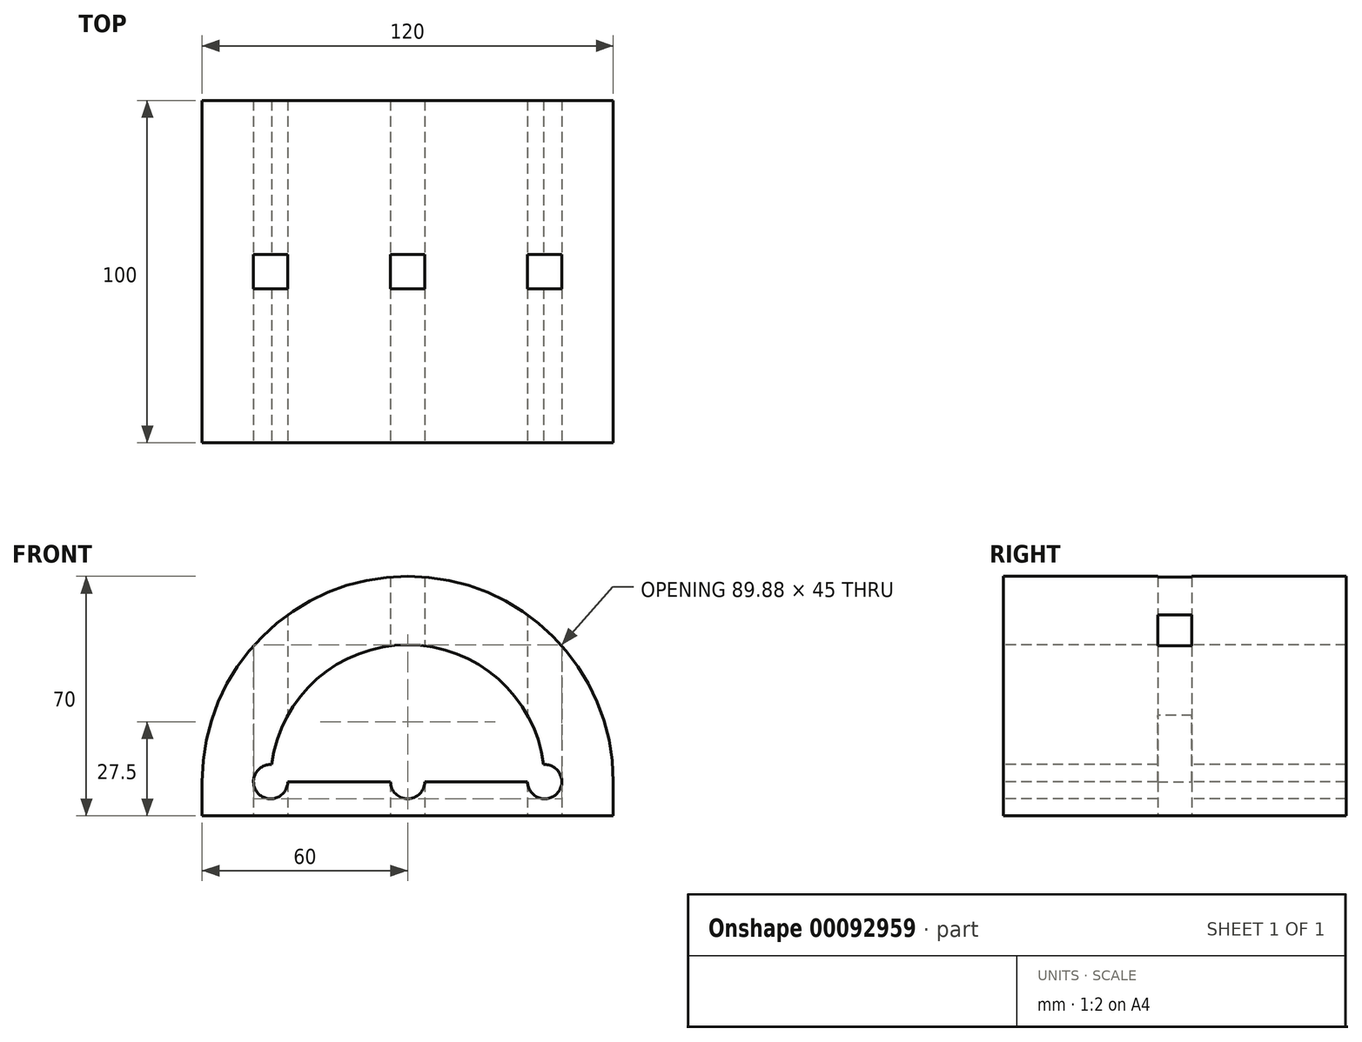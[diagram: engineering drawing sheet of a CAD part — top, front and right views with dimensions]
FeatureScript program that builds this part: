
annotation { "Feature Type Name" : "Feature", "Feature Type Description" : "" }
export const myFeature = defineFeature(function(context is Context, id is Id, definition is map)
    precondition{}
    {
        {
            var Q0;
            Q0=qCreatedBy(makeId("Top.planeOp"),FACE);
            var sketch = newSketch(context, id + "F0", { "sketchPlane" : qUnion([Q0])});
            skLineSegment(sketch, "E0.bottom", {"start": v(60, -50) * mm, "end": v(-60, -50) * mm});
            skLineSegment(sketch, "E0.top", {"start": v(60, 50) * mm, "end": v(-60, 50) * mm});
            skLineSegment(sketch, "E0.left", {"start": v(60, -50) * mm, "end": v(60, 50) * mm});
            skLineSegment(sketch, "E0.right", {"start": v(-60, -50) * mm, "end": v(-60, 50) * mm});
            skPoint(sketch, "E0.middle", {"position": v(0, 0) * mm});
            skSolve(sketch);
        }
        {
            var Q0;
            Q0 = qSketchRegion(id + "F0", true);
            extrude(context, id + "F1", {"entities" : qUnion([Q0]), "depth" : 10 * mm});
        }
        {
            var Q0;
            Q0=makeQuery(id+"F1.opExtrude","SWEPT_FACE",FACE,{"disambiguationData":[OSD([sQuery(id+"F0.wireOp",EDGE,"E0.bottom")])]});
            var sketch = newSketch(context, id + "F2", { "sketchPlane" : qUnion([Q0])});
            skArc(sketch, "E1", {"start": v(60, 10) * mm, "mid": v(0, 70) * mm, "end": v(-60, 10) * mm});
            skLineSegment(sketch, "E2", {"start": v(-60, 10) * mm, "end": v(60, 10) * mm});
            skSolve(sketch);
        }
        {
            var Q0;
            Q0=makeQuery(id+"F2.imprint","IMPRINT",FACE,{"disambiguationData":[TD([[makeQuery(id+"F2.imprint","IMPRINT",EDGE,{"derivedFrom":sQuery(id+"F2.wireOp",EDGE,"E1")}),1.0]])]});
            var Q1;
            Q1=makeQuery(id+"F1.opExtrude","SWEPT_FACE",FACE,{"disambiguationData":[OSD([sQuery(id+"F0.wireOp",EDGE,"E0.top")])]});
            extrude(context, id + "F3", {"entities" : qUnion([Q0]), "operationType" : NewBodyOperationType.ADD, "endBound" : BoundingType.UP_TO_SURFACE, "oppositeDirection" : true, "endBoundEntityFace" : qUnion([Q1]), "depth" : 25 * mm});
        }
        {
            var Q0;
            Q0=makeQuery(id+"F3.boolean.opBoolean","MERGE",FACE,{"derivedFrom":[makeQuery(id+"F1.opExtrude","SWEPT_FACE",FACE,{"disambiguationData":[OSD([sQuery(id+"F0.wireOp",EDGE,"E0.bottom")])]}),makeQuery(id+"F3.opExtrude","CAP_FACE",FACE,{"disambiguationData":[OSD([sQuery(id+"F2.wireOp",EDGE,"E1"),sQuery(id+"F2.wireOp",EDGE,"E2")])],"isStart":true})]});
            var sketch = newSketch(context, id + "F4", { "sketchPlane" : qUnion([Q0])});
            skCircle(sketch, "E3", {"center": v(0, 10) * mm, "radius": 5 * mm});
            skCircle(sketch, "E4", {"center": v(40, 10) * mm, "radius": 5 * mm});
            skCircle(sketch, "E5", {"center": v(-40, 10) * mm, "radius": 5 * mm});
            skArc(sketch, "E6", {"start": v(40, 10) * mm, "mid": v(0, 50) * mm, "end": v(-40, 10) * mm});
            skLineSegment(sketch, "E7", {"start": v(-40, 10) * mm, "end": v(40, 10) * mm});
            skSolve(sketch);
        }
        {
            var Q0;
            Q0 = qSketchRegion(id + "F4", true);
            extrude(context, id + "F5", {"entities" : qUnion([Q0]), "operationType" : NewBodyOperationType.REMOVE, "endBound" : BoundingType.THROUGH_ALL, "oppositeDirection" : true, "depth" : 25 * mm});
        }
        {
            var Q0;
            Q0=makeQuery(id+"F1.opExtrude","CAP_FACE",FACE,{"disambiguationData":[OSD([sQuery(id+"F0.wireOp",EDGE,"E0.bottom"),sQuery(id+"F0.wireOp",EDGE,"E0.top"),sQuery(id+"F0.wireOp",EDGE,"E0.left"),sQuery(id+"F0.wireOp",EDGE,"E0.right")])],"isStart":true});
            var sketch = newSketch(context, id + "F6", { "sketchPlane" : qUnion([Q0])});
            skLineSegment(sketch, "E8.bottom", {"start": v(5, 5) * mm, "end": v(-5, 5) * mm});
            skLineSegment(sketch, "E8.top", {"start": v(5, -5) * mm, "end": v(-5, -5) * mm});
            skLineSegment(sketch, "E8.left", {"start": v(5, 5) * mm, "end": v(5, -5) * mm});
            skLineSegment(sketch, "E8.right", {"start": v(-5, 5) * mm, "end": v(-5, -5) * mm});
            skPoint(sketch, "E8.middle", {"position": v(0, 0) * mm});
            skPoint(sketch, "E9.middle.positionSnap0", {"position": v(0, 5) * mm});
            skPoint(sketch, "E9.cornerSnap0", {"position": v(5, 0) * mm});
            skPoint(sketch, "E9.centerSnap0", {"position": v(0, 5) * mm});
            skLineSegment(sketch, "E10.bottom", {"start": v(45, 5) * mm, "end": v(35, 5) * mm});
            skLineSegment(sketch, "E10.top", {"start": v(45, -5) * mm, "end": v(35, -5) * mm});
            skLineSegment(sketch, "E10.left", {"start": v(45, 5) * mm, "end": v(45, -5) * mm});
            skLineSegment(sketch, "E10.right", {"start": v(35, 5) * mm, "end": v(35, -5) * mm});
            skPoint(sketch, "E10.middle", {"position": v(40, 0) * mm});
            skLineSegment(sketch, "E11.bottom", {"start": v(-35, 5) * mm, "end": v(-45, 5) * mm});
            skLineSegment(sketch, "E11.top", {"start": v(-35, -5) * mm, "end": v(-45, -5) * mm});
            skLineSegment(sketch, "E11.left", {"start": v(-35, 5) * mm, "end": v(-35, -5) * mm});
            skLineSegment(sketch, "E11.right", {"start": v(-45, 5) * mm, "end": v(-45, -5) * mm});
            skPoint(sketch, "E11.middle", {"position": v(-40, 0) * mm});
            skPoint(sketch, "E11.middle.positionSnap0", {"position": v(-5, 0) * mm});
            skPoint(sketch, "E11.centerSnap0", {"position": v(-5, 0) * mm});
            skSolve(sketch);
        }
        {
            var Q0;
            Q0 = qSketchRegion(id + "F6", true);
            extrude(context, id + "F7", {"entities" : qUnion([Q0]), "operationType" : NewBodyOperationType.REMOVE, "endBound" : BoundingType.THROUGH_ALL, "oppositeDirection" : true, "depth" : 25 * mm});
        }
    });
